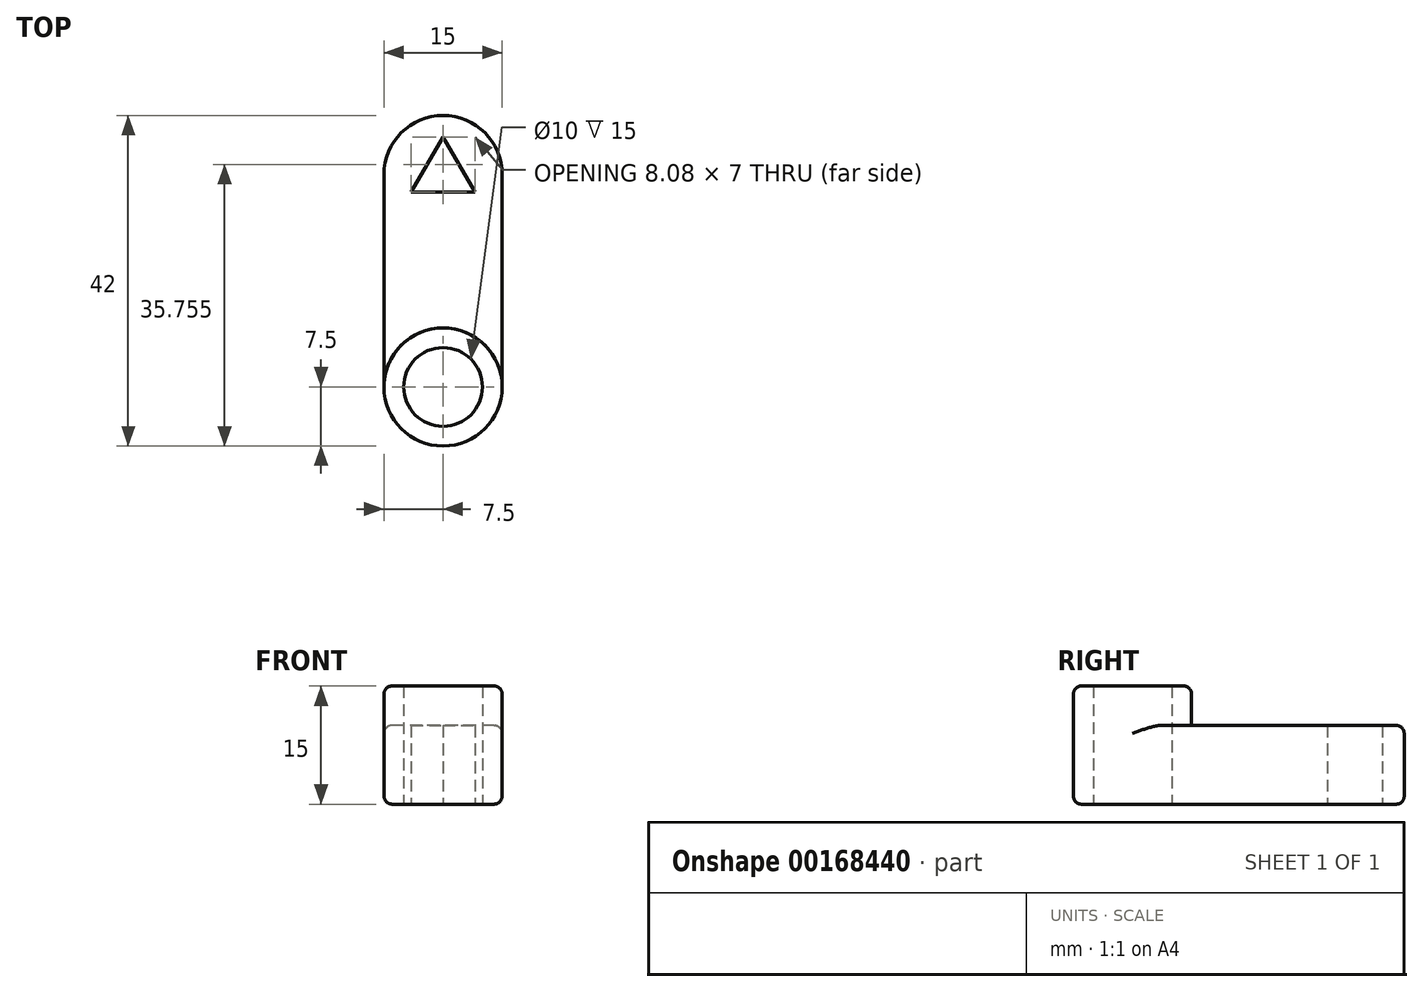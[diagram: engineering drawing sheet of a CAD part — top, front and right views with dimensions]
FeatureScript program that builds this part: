
annotation { "Feature Type Name" : "Feature", "Feature Type Description" : "" }
export const myFeature = defineFeature(function(context is Context, id is Id, definition is map)
    precondition{}
    {
        {
            var Q0;
            Q0=qCreatedBy(makeId("Top.planeOp"),FACE);
            var sketch = newSketch(context, id + "F0", { "sketchPlane" : qUnion([Q0])});
            skLineSegment(sketch, "E0.left", {"start": v(-7.5, 13.5) * mm, "end": v(-7.5, -13.5) * mm});
            skLineSegment(sketch, "E0.right", {"start": v(7.5, 25.33) * mm, "end": v(7.5, -13.5) * mm});
            skArc(sketch, "E1", {"start": v(-7.5, -13.5) * mm, "mid": v(0, -21) * mm, "end": v(7.5, -13.5) * mm});
            skPoint(sketch, "E1.centerSnap0", {"position": v(0, -13.5) * mm});
            skCircle(sketch, "E2", {"center": v(0, -13.5) * mm, "radius": 5 * mm});
            skLineSegment(sketch, "E3", {"start": v(-7.5, 13.5) * mm, "end": v(7.5, -13.5) * mm, "construction": true});
            skCircle(sketch, "E4", {"center": v(0, 13.5) * mm, "radius": 7.5 * mm});
            skLineSegment(sketch, "E5", {"start": v(0, 18.25) * mm, "end": v(4.04, 11.25) * mm});
            skLineSegment(sketch, "E6", {"start": v(4.04, 11.25) * mm, "end": v(-4.04, 11.25) * mm});
            skLineSegment(sketch, "E7", {"start": v(-4.04, 11.25) * mm, "end": v(0, 18.25) * mm});
            skLineSegment(sketch, "E8", {"start": v(-4.04, 11.25) * mm, "end": v(2.08, 14.65) * mm, "construction": true});
            skSolve(sketch);
        }
        {
            var Q0;
            Q0 = qSketchRegion(id + "F0", true);
            extrude(context, id + "F1", {"entities" : qUnion([Q0]), "depth" : 10 * mm});
        }
        {
            var Q0;
            Q0=makeQuery(id+"F1.opExtrude","CAP_FACE",FACE,{"disambiguationData":[OSD([sQuery(id+"F0.wireOp",EDGE,"E0.left"),sQuery(id+"F0.wireOp",EDGE,"E0.right"),sQuery(id+"F0.wireOp",EDGE,"E1"),sQuery(id+"F0.wireOp",EDGE,"E2"),sQuery(id+"F0.wireOp",EDGE,"E4"),sQuery(id+"F0.wireOp",EDGE,"E5"),sQuery(id+"F0.wireOp",EDGE,"E6"),sQuery(id+"F0.wireOp",EDGE,"E7")])],"isStart":false});
            var sketch = newSketch(context, id + "F2", { "sketchPlane" : qUnion([Q0])});
            skCircle(sketch, "E9", {"center": v(0, -13.5) * mm, "radius": 5 * mm});
            skCircle(sketch, "E10", {"center": v(0, -13.5) * mm, "radius": 7.5 * mm});
            skSolve(sketch);
        }
        {
            var Q0;
            Q0 = qSketchRegion(id + "F2", true);
            extrude(context, id + "F3", {"entities" : qUnion([Q0]), "operationType" : NewBodyOperationType.ADD, "depth" : 5 * mm});
        }
        {
            var Q0;
            Q0=makeQuery(id+"F1.opExtrude","CAP_EDGE",EDGE,{"disambiguationData":[OSD([sQuery(id+"F0.wireOp",EDGE,"E0.right")])],"isStart":true});
            var Q1;
            Q1=makeQuery(id+"F3.opExtrude","CAP_EDGE",EDGE,{"disambiguationData":[OSD([sQuery(id+"F2.wireOp",EDGE,"E10")])],"isStart":false});
            var Q2;
            Q2=makeQuery(id+"F1.opExtrude","CAP_EDGE",EDGE,{"disambiguationData":[OSD([sQuery(id+"F0.wireOp",EDGE,"E0.left")])],"isStart":false});
            var Q3;
            Q3=makeQuery(id+"F3.opExtrude","CAP_EDGE",EDGE,{"disambiguationData":[OSD([sQuery(id+"F2.wireOp",EDGE,"E10")])],"isStart":true});
            fillet(context, id + "F4", {"entities" : qUnion([Q0, Q1, Q2, Q3]), "radius" : 1 * mm, "tangentPropagation" : true, "allowEdgeOverflow" : false});
        }
    });
